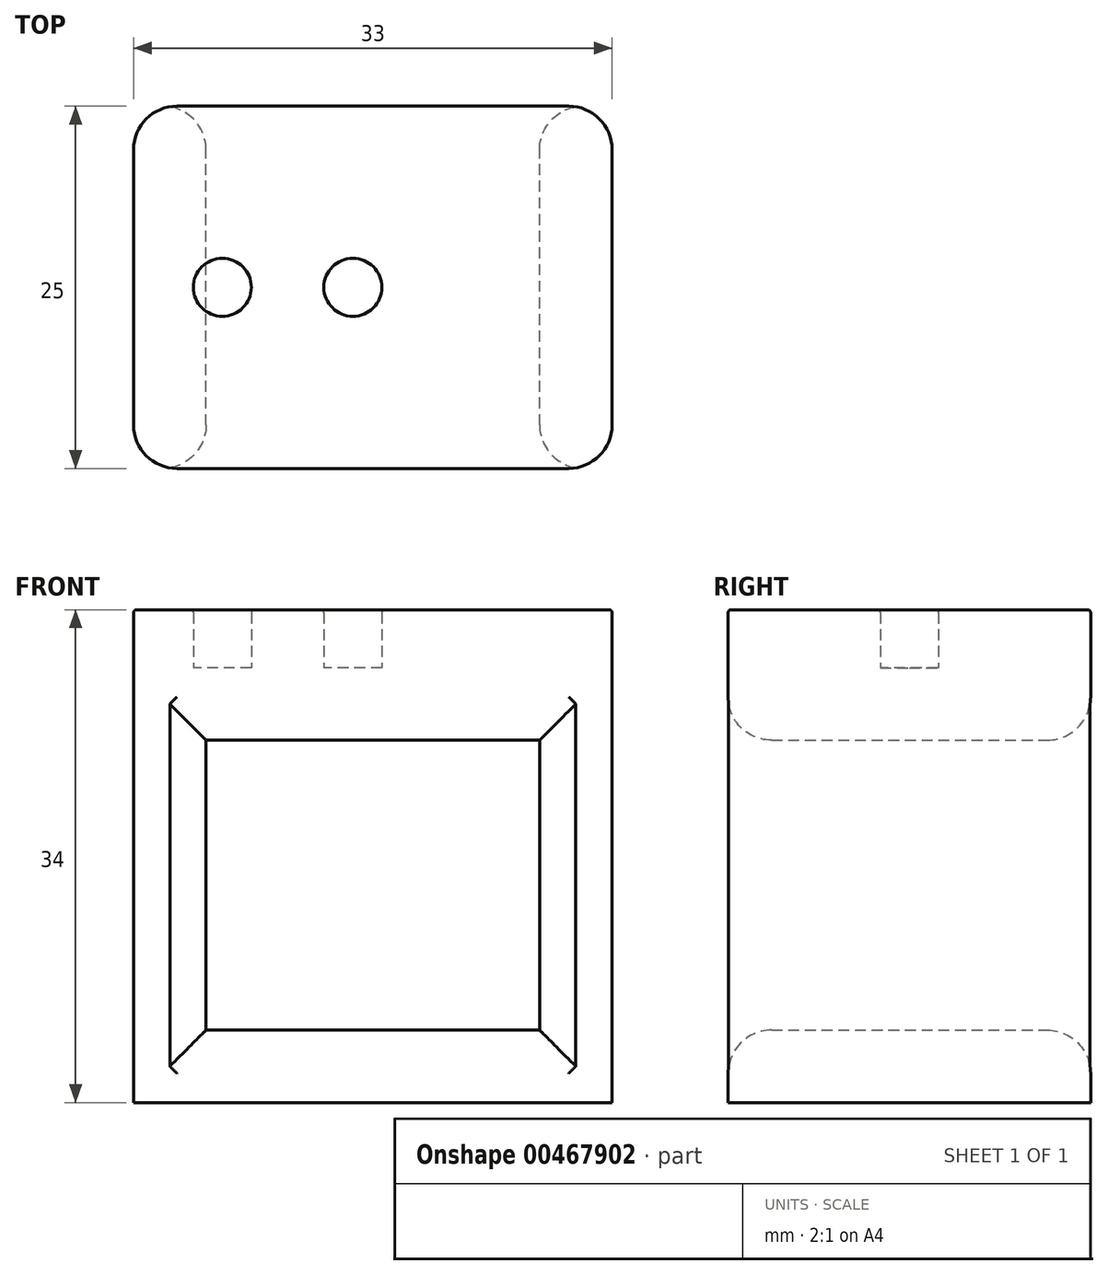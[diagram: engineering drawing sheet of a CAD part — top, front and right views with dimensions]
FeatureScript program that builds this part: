
annotation { "Feature Type Name" : "Feature", "Feature Type Description" : "" }
export const myFeature = defineFeature(function(context is Context, id is Id, definition is map)
    precondition{}
    {
        {
            var Q0;
            Q0=qCreatedBy(makeId("Front.planeOp"),FACE);
            var sketch = newSketch(context, id + "F0", { "sketchPlane" : qUnion([Q0])});
            skLineSegment(sketch, "E0.bottom", {"start": v(-16.5, 15) * mm, "end": v(16.5, 15) * mm});
            skLineSegment(sketch, "E0.top", {"start": v(-16.5, -15) * mm, "end": v(16.5, -15) * mm});
            skLineSegment(sketch, "E0.left", {"start": v(-16.5, 15) * mm, "end": v(-16.5, -15) * mm});
            skLineSegment(sketch, "E0.right", {"start": v(16.5, 15) * mm, "end": v(16.5, -15) * mm});
            skPoint(sketch, "E0.middle", {"position": v(0, 0) * mm});
            skLineSegment(sketch, "E1.bottom", {"start": v(-11.5, 10) * mm, "end": v(11.5, 10) * mm});
            skLineSegment(sketch, "E1.top", {"start": v(-11.5, -10) * mm, "end": v(11.5, -10) * mm});
            skLineSegment(sketch, "E1.left", {"start": v(-11.5, 10) * mm, "end": v(-11.5, -10) * mm});
            skLineSegment(sketch, "E1.right", {"start": v(11.5, 10) * mm, "end": v(11.5, -10) * mm});
            skSolve(sketch);
        }
        {
            var Q0;
            Q0=makeQuery(id+"F0.imprint","IMPRINT",FACE,{"disambiguationData":[TD([[makeQuery(id+"F0.imprint","IMPRINT",EDGE,{"derivedFrom":sQuery(id+"F0.wireOp",EDGE,"E0.bottom")}),-1.0]])]});
            extrude(context, id + "F1", {"entities" : qUnion([Q0]), "depth" : 25 * mm});
        }
        {
            var Q0;
            Q0=makeQuery(id+"F1.opExtrude","SWEPT_FACE",FACE,{"disambiguationData":[OSD([sQuery(id+"F0.wireOp",EDGE,"E0.bottom")])]});
            var sketch = newSketch(context, id + "F2", { "sketchPlane" : qUnion([Q0])});
            skLineSegment(sketch, "E2", {"start": v(-16.5, -12.5) * mm, "end": v(16.5, -12.5) * mm});
            skCircle(sketch, "E3", {"center": v(-10.38, -12.5) * mm, "radius": 2 * mm});
            skCircle(sketch, "E4", {"center": v(-1.38, -12.5) * mm, "radius": 2 * mm});
            skSolve(sketch);
        }
        {
            var Q0;
            {var subQ0=sQuery(id+"F2.wireOp",EDGE,"E3");var subQ1=sQuery(id+"F2.wireOp",EDGE,"E2");var subQ2=makeQuery(id+"F2.imprint","INTERSECT",VERTEX,{"disambiguationData":[OD(0.0)],"derivedFrom":[subQ1,subQ0]});Q0=makeQuery(id+"F2.imprint","IMPRINT",FACE,{"disambiguationData":[TD([[makeQuery(id+"F2.imprint","IMPRINT",EDGE,{"disambiguationData":[TD([[subQ2,-1.0]])],"derivedFrom":subQ1}),1.0]])]});}
            var Q1;
            {var subQ0=sQuery(id+"F2.wireOp",EDGE,"E3");var subQ1=sQuery(id+"F2.wireOp",EDGE,"E2");var subQ2=makeQuery(id+"F2.imprint","INTERSECT",VERTEX,{"disambiguationData":[OD(0.0)],"derivedFrom":[subQ1,subQ0]});Q1=makeQuery(id+"F2.imprint","IMPRINT",FACE,{"disambiguationData":[TD([[makeQuery(id+"F2.imprint","IMPRINT",EDGE,{"disambiguationData":[TD([[subQ2,-1.0]])],"derivedFrom":subQ1}),-1.0]])]});}
            var Q2;
            {var subQ0=sQuery(id+"F2.wireOp",EDGE,"E4");var subQ1=sQuery(id+"F2.wireOp",EDGE,"E2");var subQ2=makeQuery(id+"F2.imprint","INTERSECT",VERTEX,{"disambiguationData":[OD(0.0)],"derivedFrom":[subQ1,subQ0]});Q2=makeQuery(id+"F2.imprint","IMPRINT",FACE,{"disambiguationData":[TD([[makeQuery(id+"F2.imprint","IMPRINT",EDGE,{"disambiguationData":[TD([[subQ2,-1.0]])],"derivedFrom":subQ1}),1.0]])]});}
            var Q3;
            {var subQ0=sQuery(id+"F2.wireOp",EDGE,"E4");var subQ1=sQuery(id+"F2.wireOp",EDGE,"E2");var subQ2=makeQuery(id+"F2.imprint","INTERSECT",VERTEX,{"disambiguationData":[OD(0.0)],"derivedFrom":[subQ1,subQ0]});Q3=makeQuery(id+"F2.imprint","IMPRINT",FACE,{"disambiguationData":[TD([[makeQuery(id+"F2.imprint","IMPRINT",EDGE,{"disambiguationData":[TD([[subQ2,-1.0]])],"derivedFrom":subQ1}),-1.0]])]});}
            extrude(context, id + "F3", {"entities" : qUnion([Q0, Q1, Q2, Q3]), "operationType" : NewBodyOperationType.ADD, "depth" : 4 * mm});
        }
        {
            var Q0;
            Q0=makeQuery(id+"F3.opExtrude","CAP_FACE",FACE,{"disambiguationData":[OSD([sQuery(id+"F2.wireOp",EDGE,"E3")])],"isStart":false});
            var Q1;
            Q1=makeQuery(id+"F3.opExtrude","CAP_FACE",FACE,{"disambiguationData":[OSD([sQuery(id+"F2.wireOp",EDGE,"E4")])],"isStart":false});
            fillet(context, id + "F4", {"entities" : qUnion([Q0, Q1]), "radius" : .2 * mm, "tangentPropagation" : true, "allowEdgeOverflow" : false});
        }
        {
            var Q0;
            Q0=makeQuery(id+"F1.opExtrude","CAP_EDGE",EDGE,{"disambiguationData":[OSD([sQuery(id+"F0.wireOp",EDGE,"E1.left")])],"isStart":false});
            var Q1;
            Q1=makeQuery(id+"F1.opExtrude","CAP_EDGE",EDGE,{"disambiguationData":[OSD([sQuery(id+"F0.wireOp",EDGE,"E1.bottom")])],"isStart":false});
            var Q2;
            Q2=makeQuery(id+"F1.opExtrude","CAP_EDGE",EDGE,{"disambiguationData":[OSD([sQuery(id+"F0.wireOp",EDGE,"E1.right")])],"isStart":false});
            var Q3;
            Q3=makeQuery(id+"F1.opExtrude","CAP_EDGE",EDGE,{"disambiguationData":[OSD([sQuery(id+"F0.wireOp",EDGE,"E1.top")])],"isStart":false});
            var Q4;
            Q4=makeQuery(id+"F1.opExtrude","CAP_EDGE",EDGE,{"disambiguationData":[OSD([sQuery(id+"F0.wireOp",EDGE,"E1.left")])],"isStart":true});
            var Q5;
            Q5=makeQuery(id+"F1.opExtrude","CAP_EDGE",EDGE,{"disambiguationData":[OSD([sQuery(id+"F0.wireOp",EDGE,"E1.bottom")])],"isStart":true});
            var Q6;
            Q6=makeQuery(id+"F1.opExtrude","CAP_EDGE",EDGE,{"disambiguationData":[OSD([sQuery(id+"F0.wireOp",EDGE,"E1.top")])],"isStart":true});
            var Q7;
            Q7=makeQuery(id+"F1.opExtrude","CAP_EDGE",EDGE,{"disambiguationData":[OSD([sQuery(id+"F0.wireOp",EDGE,"E1.right")])],"isStart":true});
            var Q8;
            Q8=makeQuery(id+"F1.opExtrude","CAP_EDGE",EDGE,{"disambiguationData":[OSD([sQuery(id+"F0.wireOp",EDGE,"E0.bottom")])],"isStart":true});
            var Q9;
            Q9=makeQuery(id+"F1.opExtrude","CAP_EDGE",EDGE,{"disambiguationData":[OSD([sQuery(id+"F0.wireOp",EDGE,"E0.right")])],"isStart":true});
            var Q10;
            Q10=makeQuery(id+"F1.opExtrude","CAP_EDGE",EDGE,{"disambiguationData":[OSD([sQuery(id+"F0.wireOp",EDGE,"E0.left")])],"isStart":true});
            var Q11;
            Q11=makeQuery(id+"F1.opExtrude","SWEPT_EDGE",EDGE,{"disambiguationData":[OSD([sQuery(id+"F0.wireOp",EDGE,"E0.bottom"),sQuery(id+"F0.wireOp",EDGE,"E0.left")])]});
            var Q12;
            Q12=makeQuery(id+"F1.opExtrude","CAP_EDGE",EDGE,{"disambiguationData":[OSD([sQuery(id+"F0.wireOp",EDGE,"E0.bottom")])],"isStart":false});
            var Q13;
            Q13=makeQuery(id+"F1.opExtrude","CAP_EDGE",EDGE,{"disambiguationData":[OSD([sQuery(id+"F0.wireOp",EDGE,"E0.left")])],"isStart":false});
            var Q14;
            Q14=makeQuery(id+"F1.opExtrude","CAP_EDGE",EDGE,{"disambiguationData":[OSD([sQuery(id+"F0.wireOp",EDGE,"E0.right")])],"isStart":false});
            var Q15;
            Q15=makeQuery(id+"F1.opExtrude","SWEPT_EDGE",EDGE,{"disambiguationData":[OSD([sQuery(id+"F0.wireOp",EDGE,"E0.bottom"),sQuery(id+"F0.wireOp",EDGE,"E0.right")])]});
            fillet(context, id + "F5", {"entities" : qUnion([Q0, Q1, Q2, Q3, Q4, Q5, Q6, Q7, Q8, Q9, Q10, Q11, Q12, Q13, Q14, Q15]), "radius" : 3 * mm, "tangentPropagation" : true, "allowEdgeOverflow" : false});
        }
    });
